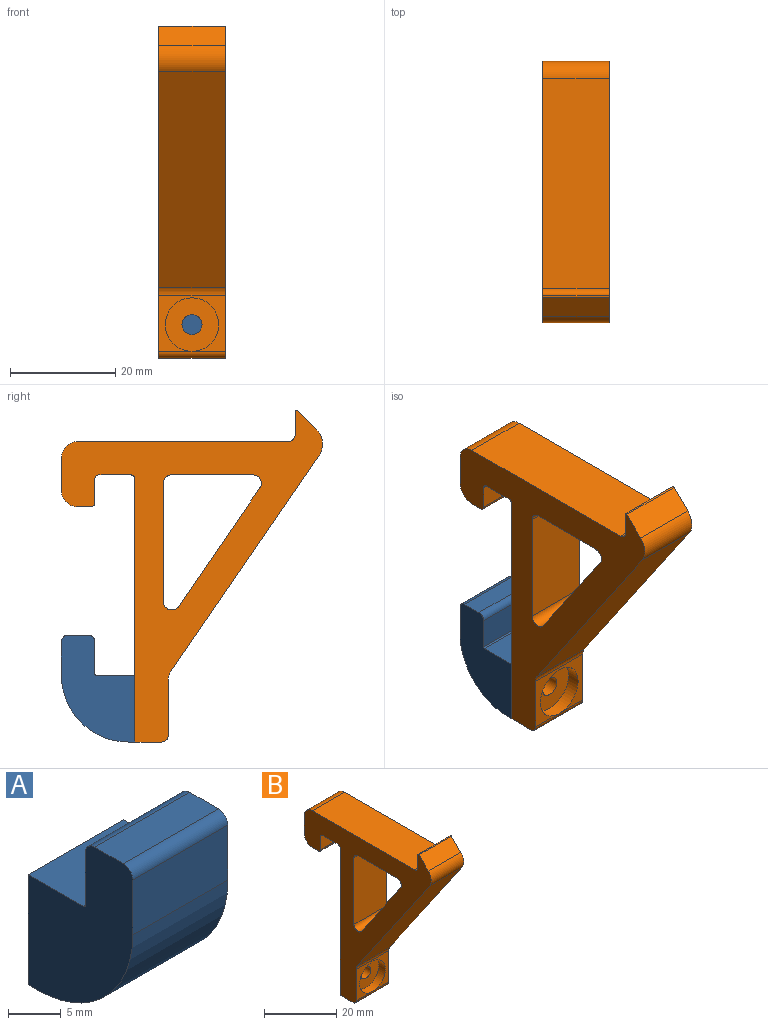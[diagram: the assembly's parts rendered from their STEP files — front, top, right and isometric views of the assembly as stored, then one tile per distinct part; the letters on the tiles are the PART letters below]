
ASSEMBLY  parts=2 mates=1
PART A: 14 faces, bbox 12.7x14x20.3 mm
  f0: plane 20.32x13.97mm, normal (1,0,0), area 190.5mm2, adj f1,f3,f5,f7,f8,f9,f10,f11
  f1: plane 12.7x7.37mm, normal (0,0,1), area 93.5mm2, adj f0,f2,f5,f11
  f2: plane 20.32x13.97mm, normal (-1,0,0), area 190.5mm2, adj f1,f3,f5,f7,f8,f9,f10,f11
  f3: plane 12.7x1.27mm, normal (0,0,-1), area 16.1mm2, adj f0,f2,f5,f10
  f4: cylinder r=1.91mm len=7.62mm, axis (0,1,0), area 91.2mm2, adj f5,f6
  f5: plane 12.7x12.7mm, normal (0,1,0), area 149.9mm2, adj f0,f1,f2,f3,f4
  f6: plane 3.81x3.81mm, normal (0,1,0), area 11.4mm2, adj f4
  f7: plane 12.7x3.81mm, normal (0,0,1), area 48.4mm2, adj f0,f2,f12,f13
  f8: plane 12.7x6.35mm, normal (0,-1,0), area 80.6mm2, adj f0,f2,f10,f13
  f9: plane 12.7x6.1mm, normal (0,1,0), area 77.4mm2, adj f0,f2,f11,f12
  f10: cylinder r=12.7mm len=12.7mm, axis (-1,0,0), area 253.4mm2, adj f0,f2,f3,f8
  f11: cylinder r=0.25mm len=12.7mm, axis (1,0,0), area 5.1mm2, adj f0,f1,f2,f9
  f12: cylinder r=1.27mm len=12.7mm, axis (-1,0,0), area 25.3mm2, adj f0,f2,f7,f9
  f13: cylinder r=1.27mm len=12.7mm, axis (1,0,0), area 25.3mm2, adj f0,f2,f7,f8
PART B: 32 faces, bbox 12.7x49.7x63.1 mm
  f0: cylinder r=1.59mm len=12.7mm, axis (-1,0,0), area 43.8mm2, adj f1,f23,f24,f25
  f1: plane 15.44x12.7mm, normal (0,0,-1), area 196.1mm2, adj f0,f2,f24,f25
  f2: cylinder r=1.59mm len=12.7mm, axis (-1,0,0), area 31.7mm2, adj f1,f3,f24,f25
  f3: plane 22.51x12.7mm, normal (0,-1,0), area 285.9mm2, adj f2,f4,f24,f25
  f4: cylinder r=1.59mm len=12.7mm, axis (-1,0,0), area 51.2mm2, adj f3,f23,f24,f25
  f5: cylinder r=0.79mm len=12.7mm, axis (-1,0,0), area 15.8mm2, adj f6,f22,f24,f25
  f6: plane 12.7x4.51mm, normal (0,-1,0), area 57.3mm2, adj f5,f24,f25,f31
  f7: plane 12.7x2.38mm, normal (0,0,-1), area 30.2mm2, adj f8,f24,f25,f31
  f8: cylinder r=3.17mm len=12.7mm, axis (-1,0,0), area 63.3mm2, adj f7,f9,f24,f25
  f9: plane 12.7x6.1mm, normal (0,1,0), area 77.4mm2, adj f8,f10,f24,f25
  f10: cylinder r=3.17mm len=12.7mm, axis (-1,0,0), area 63.3mm2, adj f9,f11,f24,f25
  f11: plane 40.01x12.7mm, normal (0,0,1), area 508.1mm2, adj f10,f12,f24,f25
  f12: cylinder r=1.27mm len=12.7mm, axis (-1,0,0), area 25.3mm2, adj f11,f13,f24,f25
  f13: plane 12.7x4.47mm, normal (0,1,0), area 56.7mm2, adj f12,f14,f24,f25
  f14: cylinder r=0.25mm len=12.7mm, axis (-1,0,0), area 7.6mm2, adj f13,f15,f24,f25
  f15: plane 12.7x3.68mm, normal (0,-0.71,0.71), area 66.1mm2, adj f14,f16,f24,f25
  f16: cylinder r=3.81mm len=12.7mm, axis (-1,0,0), area 67.1mm2, adj f15,f17,f24,f25
  f17: plane 41.19x28.24mm, normal (0,-0.82,-0.57), area 634.3mm2, adj f16,f24,f25,f29
  f18: plane 12.7x10.64mm, normal (0,-1,0), area 54.1mm2, adj f24,f25,f26,f29,f30
  f19: plane 12.7x5.08mm, normal (0,0,-1), area 64.5mm2, adj f20,f24,f25,f30
  f20: plane 50.01x12.7mm, normal (0,1,0), area 623.7mm2, adj f19,f21,f24,f25,f28
  f21: cylinder r=0.79mm len=12.7mm, axis (-1,0,0), area 15.8mm2, adj f20,f22,f24,f25
  f22: plane 12.7x6.03mm, normal (0,0,-1), area 76.6mm2, adj f5,f21,f24,f25
  f23: plane 22.51x15.44mm, normal (0,0.82,0.57), area 346.7mm2, adj f0,f4,f24,f25
  f24: plane 63.14x49.68mm, normal (1,0,0), area 896.4mm2, adj f0,f1,f2,f3,f4,f5,f6,f7
  f25: plane 63.14x49.68mm, normal (-1,0,0), area 896.4mm2, adj f0,f1,f2,f3,f4,f5,f6,f7
  f26: cylinder r=5.08mm len=10.16mm, axis (0,-1,0), area 81.1mm2, adj f18,f27
  f27: plane 10.16x10.16mm, normal (0,-1,0), area 69.7mm2, adj f26,f28
  f28: cylinder r=1.91mm len=3.81mm, axis (0,-1,0), area 45.6mm2, adj f20,f27
  f29: cylinder r=2.54mm len=12.7mm, axis (-1,0,0), area 19.4mm2, adj f17,f18,f24,f25
  f30: cylinder r=1.27mm len=12.7mm, axis (-1,0,0), area 25.3mm2, adj f18,f19,f24,f25
  f31: cylinder r=0.79mm len=12.7mm, axis (-1,0,0), area 15.8mm2, adj f6,f7,f24,f25
PLACE A rot(axis=(0,0,1),180deg) t=(11.42,27.95,-5.83)mm
PLACE B rot(axis=(0,0,-1),0deg) t=(5.07,27.95,0.52)mm
MATE planar B.f26 <-> A.f4  axis (0,1,0) through (11.42,27.95,-5.83)mm
